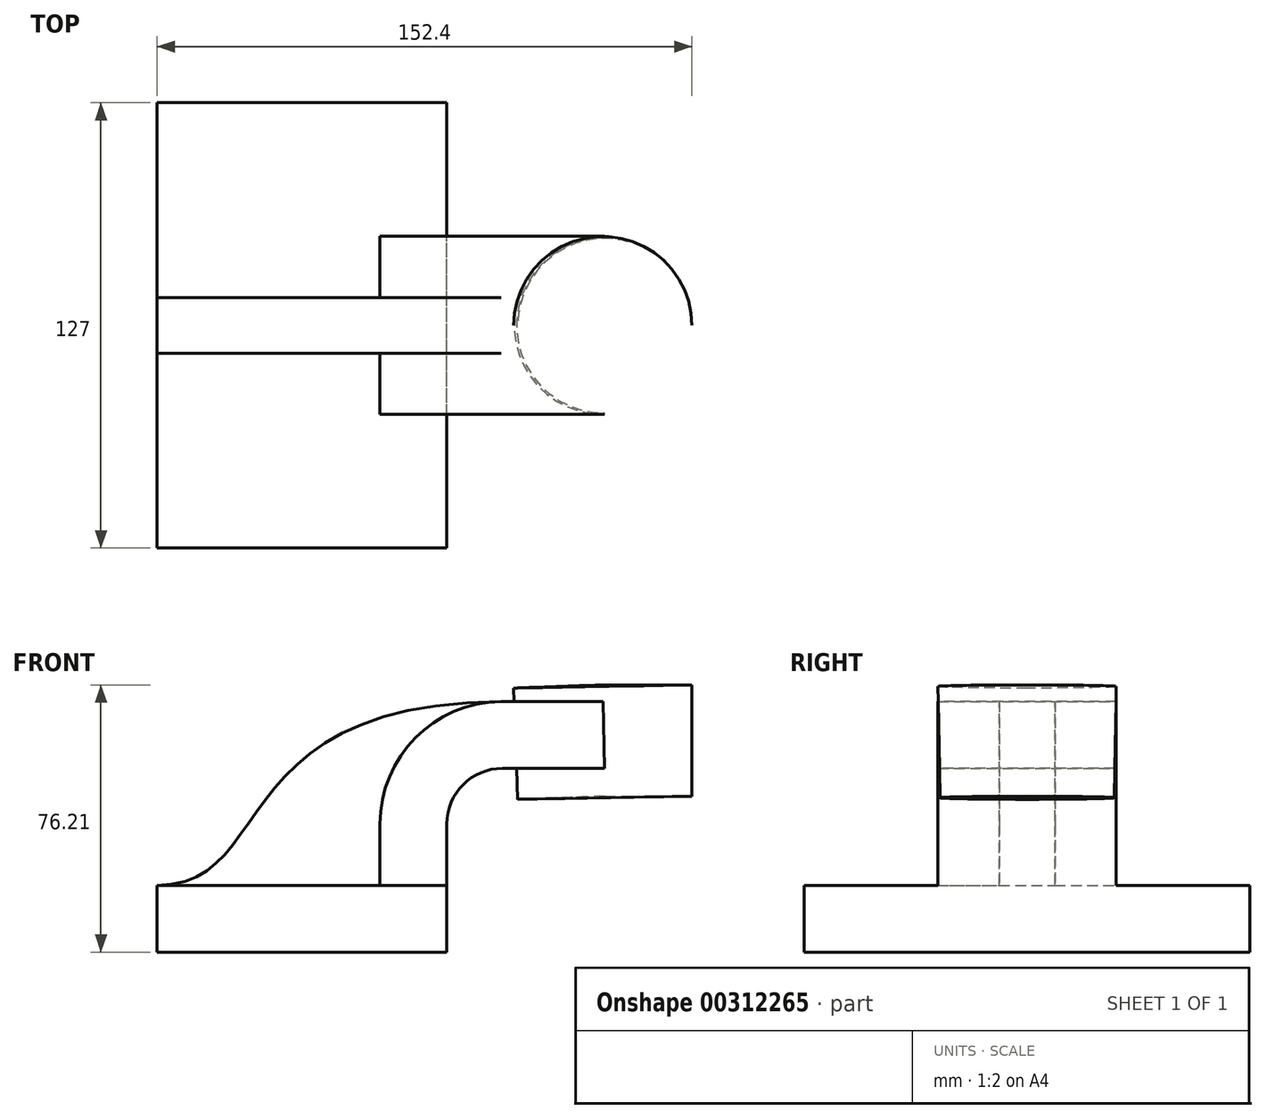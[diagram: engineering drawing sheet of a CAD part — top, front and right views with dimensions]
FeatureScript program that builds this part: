
annotation { "Feature Type Name" : "Feature", "Feature Type Description" : "" }
export const myFeature = defineFeature(function(context is Context, id is Id, definition is map)
    precondition{}
    {
        {
            var Q0;
            Q0=qCreatedBy(makeId("Front.planeOp"),FACE);
            var sketch = newSketch(context, id + "F0", { "sketchPlane" : qUnion([Q0])});
            skLineSegment(sketch, "E0.bottom", {"start": v(-18.52, 9.52) * mm, "end": v(64.03, 9.53) * mm});
            skLineSegment(sketch, "E0.top", {"start": v(-18.52, -9.53) * mm, "end": v(64.03, -9.52) * mm});
            skLineSegment(sketch, "E0.left", {"start": v(-18.52, 9.52) * mm, "end": v(-18.52, -9.53) * mm});
            skLineSegment(sketch, "E0.right", {"start": v(64.03, 9.52) * mm, "end": v(64.03, -9.53) * mm});
            skPoint(sketch, "E0.middle", {"position": v(22.75, 0) * mm});
            skLineSegment(sketch, "E1", {"start": v(64.03, 9.52) * mm, "end": v(64.03, 27) * mm});
            skArc(sketch, "E2", {"start": v(64.03, 27) * mm, "mid": v(68.68, 38.23) * mm, "end": v(79.9, 42.88) * mm});
            skLineSegment(sketch, "E3.bottom", {"start": v(133.88, 66.68) * mm, "end": v(83.08, 66.68) * mm});
            skLineSegment(sketch, "E3.top", {"start": v(133.88, 34.92) * mm, "end": v(83.08, 34.92) * mm});
            skLineSegment(sketch, "E3.right", {"start": v(83.08, 66.68) * mm, "end": v(83.08, 34.92) * mm});
            skPoint(sketch, "E3.middle", {"position": v(108.48, 50.8) * mm});
            skArc(sketch, "E4.1", {"start": v(44.98, 27) * mm, "mid": v(55.2, 51.7) * mm, "end": v(79.9, 61.93) * mm});
            skLineSegment(sketch, "E5", {"start": v(133.88, 66.68) * mm, "end": v(133.88, 34.92) * mm});
            skFitSpline(sketch, "E6", {"points": [v(-18.52, 9.52) * mm, v(79.9, 61.93) * mm], "startDerivative": vector(103.16, 0) * mm, "endDerivative": vector(239.71, 1) * mm});
            skLineSegment(sketch, "E7", {"start": v(44.98, 27) * mm, "end": v(44.98, 9.52) * mm});
            skLineSegment(sketch, "E8", {"start": v(79.9, 61.93) * mm, "end": v(109.05, 61.93) * mm});
            skLineSegment(sketch, "E9", {"start": v(108.48, 66.68) * mm, "end": v(109.05, 34.92) * mm});
            skLineSegment(sketch, "E10", {"start": v(79.9, 42.88) * mm, "end": v(108.9, 42.88) * mm});
            skSolve(sketch);
        }
        {
            var Q0;
            Q0=makeQuery(id+"F0.imprint","IMPRINT",FACE,{"disambiguationData":[TD([[makeQuery(id+"F0.imprint","IMPRINT",EDGE,{"derivedFrom":sQuery(id+"F0.wireOp",EDGE,"E0.top")}),1.0]])]});
            extrude(context, id + "F1", {"entities" : qUnion([Q0]), "endBound" : BoundingType.SYMMETRIC, "depth" : 127 * mm});
        }
        {
            var Q0;
            {var subQ5=sQuery(id+"F0.wireOp",EDGE,"E1");Q0=makeQuery(id+"F0.imprint","IMPRINT",FACE,{"disambiguationData":[TD([[makeQuery(id+"F0.imprint","IMPRINT",EDGE,{"derivedFrom":subQ5}),1.0]])]});}
            var Q1;
            {var subQ0=sQuery(id+"F0.wireOp",EDGE,"E8");var subQ1=sQuery(id+"F0.wireOp",EDGE,"E3.right");var subQ2=makeQuery(id+"F0.imprint","INTERSECT",VERTEX,{"derivedFrom":[subQ1,subQ0]});Q1=makeQuery(id+"F0.imprint","IMPRINT",FACE,{"disambiguationData":[TD([[makeQuery(id+"F0.imprint","IMPRINT",EDGE,{"disambiguationData":[TD([[subQ2,-1.0]])],"derivedFrom":subQ1}),1.0]])]});}
            extrude(context, id + "F2", {"entities" : qUnion([Q0, Q1]), "operationType" : NewBodyOperationType.ADD, "endBound" : BoundingType.SYMMETRIC, "depth" : 50.8 * mm});
        }
        {
            var Q0;
            {var subQ3=sQuery(id+"F0.wireOp",EDGE,"E7");Q0=makeQuery(id+"F0.imprint","IMPRINT",FACE,{"disambiguationData":[TD([[makeQuery(id+"F0.imprint","IMPRINT",EDGE,{"derivedFrom":subQ3}),-1.0]])]});}
            extrude(context, id + "F3", {"entities" : qUnion([Q0]), "operationType" : NewBodyOperationType.ADD, "endBound" : BoundingType.SYMMETRIC, "depth" : 15.88 * mm});
        }
        {
            var Q0;
            {var subQ0=sQuery(id+"F0.wireOp",EDGE,"E5");Q0=makeQuery(id+"F0.imprint","IMPRINT",FACE,{"disambiguationData":[TD([[makeQuery(id+"F0.imprint","IMPRINT",EDGE,{"derivedFrom":subQ0}),-1.0]])]});}
            var Q1;
            Q1=sQuery(id+"F0.wireOp",EDGE,"E9");
            revolve(context, id + "F4", {"operationType" : NewBodyOperationType.ADD, "entities" : qUnion([Q0]), "axis" : qUnion([Q1]), "revolveType" : RevolveType.FULL});
        }
    });
